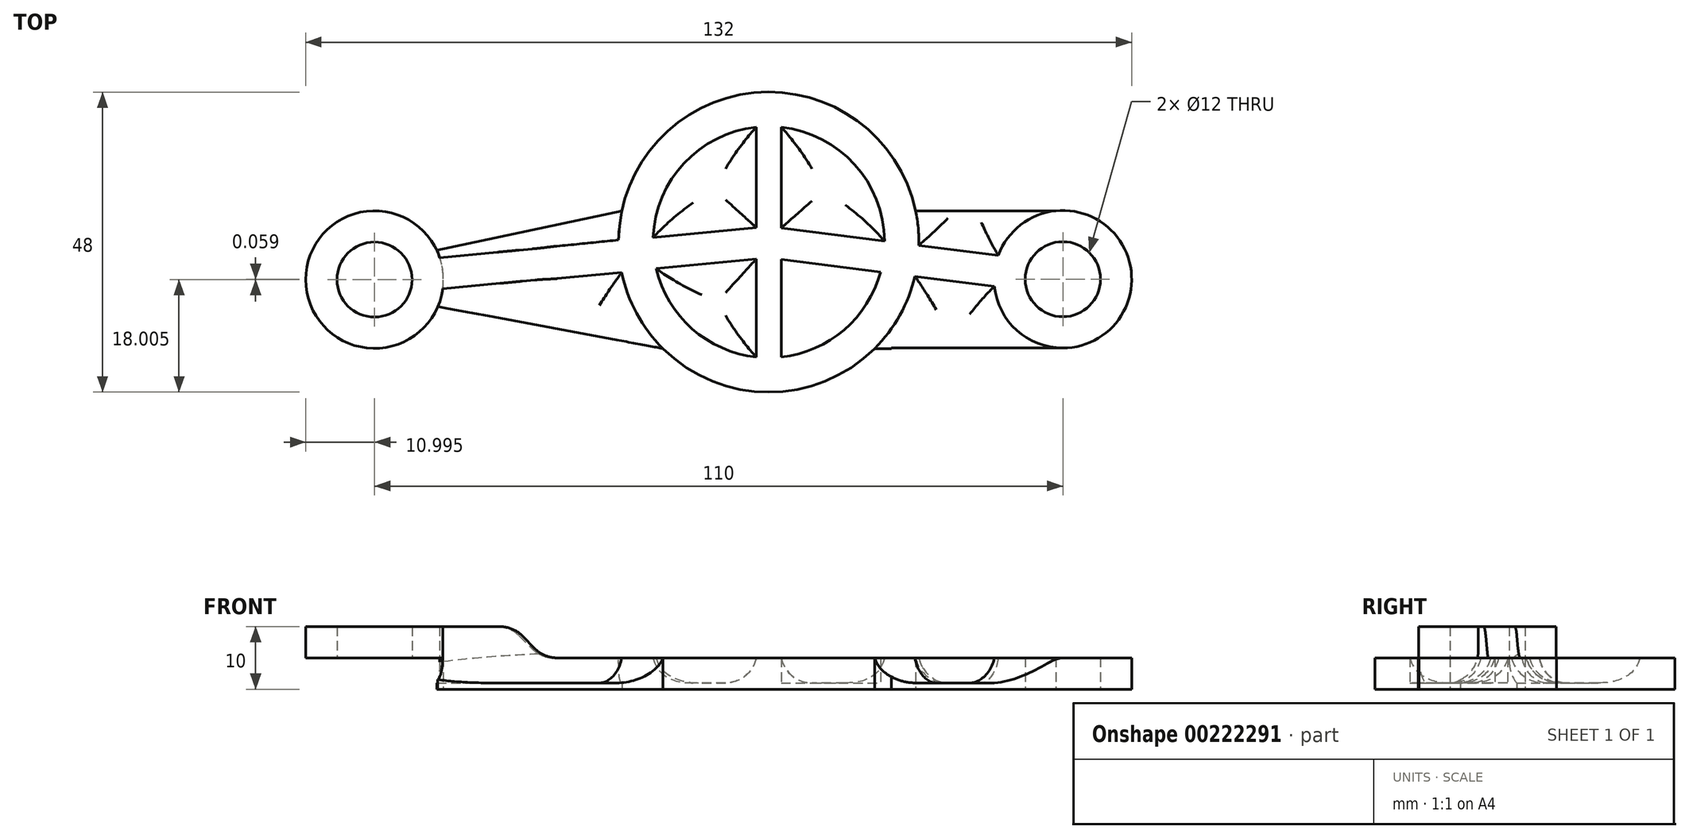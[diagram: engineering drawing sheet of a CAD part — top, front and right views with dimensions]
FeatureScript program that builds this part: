
annotation { "Feature Type Name" : "Feature", "Feature Type Description" : "" }
export const myFeature = defineFeature(function(context is Context, id is Id, definition is map)
    precondition{}
    {
        {
            var Q0;
            Q0=qCreatedBy(makeId("Top.planeOp"),FACE);
            var sketch = newSketch(context, id + "F0", { "sketchPlane" : qUnion([Q0])});
            skCircle(sketch, "E0", {"center": v(60.37, 19.35) * mm, "radius": 6 * mm});
            skLineSegment(sketch, "E1", {"start": v(-49.54, 25.3) * mm, "end": v(61.21, 25.3) * mm, "construction": true});
            skArc(sketch, "E2", {"start": v(60.37, 8.35) * mm, "mid": v(71.35, 19.93) * mm, "end": v(59.22, 30.3) * mm});
            skLineSegment(sketch, "E3.bottom", {"start": v(-10.1, 30.3) * mm, "end": v(32.97, 30.3) * mm});
            skLineSegment(sketch, "E3.top", {"start": v(-3.55, 8.27) * mm, "end": v(32.97, 8.27) * mm});
            skLineSegment(sketch, "E4.bottom", {"start": v(60.37, 8.35) * mm, "end": v(32.97, 8.35) * mm});
            skLineSegment(sketch, "E4.top", {"start": v(60.37, 30.3) * mm, "end": v(32.97, 30.3) * mm});
            skLineSegment(sketch, "E4.left", {"start": v(60.37, 25.3) * mm, "end": v(60.37, 25.35) * mm});
            skLineSegment(sketch, "E5.trimOffspring", {"start": v(32.97, 8.35) * mm, "end": v(32.97, 8.27) * mm});
            skLineSegment(sketch, "E6.trimOffspring", {"start": v(-49.63, 8.3) * mm, "end": v(-49.63, 8.27) * mm});
            skCircle(sketch, "E7", {"center": v(13.37, 25.3) * mm, "radius": 19 * mm, "construction": true});
            skArc(sketch, "E8", {"start": v(-3.55, 8.27) * mm, "mid": v(13.37, 1.3) * mm, "end": v(30.28, 8.27) * mm});
            skArc(sketch, "E9.trimOffspring", {"start": v(36.84, 30.3) * mm, "mid": v(13.37, 49.3) * mm, "end": v(-10.1, 30.3) * mm});
            skLineSegment(sketch, "E10", {"start": v(13.37, 25.3) * mm, "end": v(-49.63, 19.3) * mm, "construction": true});
            skLineSegment(sketch, "E11", {"start": v(-49.63, 19.3) * mm, "end": v(-49.4, 16.8) * mm});
            skLineSegment(sketch, "E12", {"start": v(-39.68, 23.97) * mm, "end": v(-10.1, 30.3) * mm});
            skLineSegment(sketch, "E13", {"start": v(-39.52, 14.97) * mm, "end": v(-3.55, 8.27) * mm});
            skArc(sketch, "E14", {"start": v(-39.52, 14.97) * mm, "mid": v(-38.64, 19.48) * mm, "end": v(-39.68, 23.97) * mm});
            skSolve(sketch);
        }
        {
            var Q0;
            Q0 = qSketchRegion(id + "F0", true);
            extrude(context, id + "F1", {"entities" : qUnion([Q0]), "depth" : 1 * mm});
        }
        {
            var Q0;
            Q0=makeQuery(id+"F1.opExtrude","CAP_FACE",FACE,{"disambiguationData":[OSD([sQuery(id+"F0.wireOp",EDGE,"2d779d73-95e5-4ba3-8006-2094022f3e68"),sQuery(id+"F0.wireOp",EDGE,"E0"),sQuery(id+"F0.wireOp",EDGE,"E2"),sQuery(id+"F0.wireOp",EDGE,"44cde904-ac06-42cb-a7ef-0284b28cecda"),sQuery(id+"F0.wireOp",EDGE,"E3.bottom"),sQuery(id+"F0.wireOp",EDGE,"E3.top"),sQuery(id+"F0.wireOp",EDGE,"E4.bottom"),sQuery(id+"F0.wireOp",EDGE,"E4.top"),sQuery(id+"F0.wireOp",EDGE,"E5.trimOffspring"),sQuery(id+"F0.wireOp",EDGE,"E6.trimOffspring"),sQuery(id+"F0.wireOp",EDGE,"E8"),sQuery(id+"F0.wireOp",EDGE,"E9.trimOffspring")])],"isStart":false});
            var sketch = newSketch(context, id + "F2", { "sketchPlane" : qUnion([Q0])});
            skLineSegment(sketch, "E15", {"start": v(-49.63, 19.3) * mm, "end": v(60.37, 19.35) * mm, "construction": true});
            skLineSegment(sketch, "E16", {"start": v(13.37, 1.3) * mm, "end": v(13.37, 49.3) * mm, "construction": true});
            skLineSegment(sketch, "E17", {"start": v(15.37, 43.69) * mm, "end": v(15.37, 27.56) * mm});
            skLineSegment(sketch, "E18", {"start": v(11.37, 6.9) * mm, "end": v(11.37, 22.6) * mm});
            skArc(sketch, "E19", {"start": v(-10.16, 20.54) * mm, "mid": v(13, 1.3) * mm, "end": v(36.73, 19.82) * mm});
            skArc(sketch, "E20", {"start": v(11.37, 43.69) * mm, "mid": v(-0.15, 37.93) * mm, "end": v(-5.12, 26.05) * mm});
            skLineSegment(sketch, "E21", {"start": v(13.37, 25.3) * mm, "end": v(60.37, 19.35) * mm, "construction": true});
            skLineSegment(sketch, "E22", {"start": v(13.37, 25.3) * mm, "end": v(-49.63, 19.3) * mm, "construction": true});
            skLineSegment(sketch, "E23.trimOffspring", {"start": v(11.37, 49.21) * mm, "end": v(11.37, 49.3) * mm});
            skArc(sketch, "E24.trimOffspring", {"start": v(15.37, 6.9) * mm, "mid": v(25.4, 11.25) * mm, "end": v(31.24, 20.52) * mm});
            skLineSegment(sketch, "E25", {"start": v(-39.2, 22.8) * mm, "end": v(-10.63, 25.52) * mm});
            skLineSegment(sketch, "E26", {"start": v(11.37, 22.6) * mm, "end": v(-4.65, 21.07) * mm});
            skCircle(sketch, "E27", {"center": v(-49.63, 19.3) * mm, "radius": 6 * mm});
            skArc(sketch, "E28", {"start": v(-39.2, 22.8) * mm, "mid": v(-60.59, 18.25) * mm, "end": v(-38.73, 17.82) * mm});
            skArc(sketch, "E29.trimOffspring", {"start": v(-4.65, 21.07) * mm, "mid": v(1.1, 11.44) * mm, "end": v(11.37, 6.9) * mm});
            skLineSegment(sketch, "E30.trimOffspring", {"start": v(-5.12, 26.05) * mm, "end": v(11.37, 27.62) * mm});
            skLineSegment(sketch, "E31.trimOffspring", {"start": v(-10.16, 20.54) * mm, "end": v(-38.73, 17.82) * mm});
            skLineSegment(sketch, "E32.trimOffspring", {"start": v(11.37, 27.62) * mm, "end": v(11.37, 43.69) * mm});
            skLineSegment(sketch, "E33", {"start": v(15.37, 22.52) * mm, "end": v(49.42, 18.22) * mm});
            skLineSegment(sketch, "E34.trimOffspring", {"start": v(15.37, 22.52) * mm, "end": v(15.37, 6.9) * mm});
            skArc(sketch, "E35.trimOffspring", {"start": v(31.86, 25.48) * mm, "mid": v(27.07, 37.72) * mm, "end": v(15.37, 43.69) * mm});
            skArc(sketch, "E36.trimOffspring", {"start": v(37.36, 24.78) * mm, "mid": v(13.73, 49.3) * mm, "end": v(-10.63, 25.52) * mm});
            skCircle(sketch, "E37", {"center": v(60.37, 19.35) * mm, "radius": 6 * mm});
            skArc(sketch, "E38.trimOffspring", {"start": v(49.42, 18.22) * mm, "mid": v(71.28, 17.98) * mm, "end": v(50.05, 23.18) * mm});
            skLineSegment(sketch, "E39.trimOffspring", {"start": v(50.05, 23.18) * mm, "end": v(15.37, 27.56) * mm});
            skSolve(sketch);
        }
        {
            var Q0;
            Q0=makeQuery(id+"F2.imprint","IMPRINT",FACE,{"disambiguationData":[TD([[makeQuery(id+"F2.imprint","IMPRINT",EDGE,{"derivedFrom":sQuery(id+"F2.wireOp",EDGE,"E17")}),-1.0]])]});
            extrude(context, id + "F3", {"entities" : qUnion([Q0]), "operationType" : NewBodyOperationType.ADD, "depth" : 4 * mm});
        }
        {
            var Q0;
            Q0=makeQuery(id+"F3.opExtrude","CAP_FACE",FACE,{"disambiguationData":[OSD([sQuery(id+"F2.wireOp",EDGE,"E17"),sQuery(id+"F2.wireOp",EDGE,"E18"),sQuery(id+"F2.wireOp",EDGE,"E19"),sQuery(id+"F2.wireOp",EDGE,"E20"),sQuery(id+"F2.wireOp",EDGE,"E24.trimOffspring"),sQuery(id+"F2.wireOp",EDGE,"E25"),sQuery(id+"F2.wireOp",EDGE,"E26"),sQuery(id+"F2.wireOp",EDGE,"E27"),sQuery(id+"F2.wireOp",EDGE,"E28"),sQuery(id+"F2.wireOp",EDGE,"E29.trimOffspring"),sQuery(id+"F2.wireOp",EDGE,"E30.trimOffspring"),sQuery(id+"F2.wireOp",EDGE,"E31.trimOffspring"),sQuery(id+"F2.wireOp",EDGE,"E32.trimOffspring"),sQuery(id+"F2.wireOp",EDGE,"E33"),sQuery(id+"F2.wireOp",EDGE,"E34.trimOffspring"),sQuery(id+"F2.wireOp",EDGE,"E35.trimOffspring"),sQuery(id+"F2.wireOp",EDGE,"E36.trimOffspring"),sQuery(id+"F2.wireOp",EDGE,"E37"),sQuery(id+"F2.wireOp",EDGE,"E38.trimOffspring"),sQuery(id+"F2.wireOp",EDGE,"E39.trimOffspring")])],"isStart":false});
            var sketch = newSketch(context, id + "F4", { "sketchPlane" : qUnion([Q0])});
            skCircle(sketch, "E40", {"center": v(-49.63, 19.3) * mm, "radius": 6 * mm});
            skArc(sketch, "E41", {"start": v(-39.2, 22.8) * mm, "mid": v(-60.59, 18.25) * mm, "end": v(-38.73, 17.82) * mm});
            skLineSegment(sketch, "E42", {"start": v(-38.73, 17.82) * mm, "end": v(-22.52, 19.37) * mm});
            skLineSegment(sketch, "E43", {"start": v(-22.52, 19.37) * mm, "end": v(-23, 24.34) * mm});
            skLineSegment(sketch, "E44", {"start": v(-23, 24.34) * mm, "end": v(-39.2, 22.8) * mm});
            skSolve(sketch);
        }
        {
            var Q0;
            Q0 = qSketchRegion(id + "F4", true);
            extrude(context, id + "F5", {"entities" : qUnion([Q0]), "operationType" : NewBodyOperationType.ADD, "depth" : 5 * mm});
        }
        {
            var Q0;
            Q0=makeQuery(id+"F5.opExtrude","CAP_EDGE",EDGE,{"disambiguationData":[OSD([sQuery(id+"F4.wireOp",EDGE,"E43")])],"isStart":false});
            chamfer(context, id + "F6", {"entities" : qUnion([Q0]), "width" : 5 * mm, "tangentPropagation" : true});
        }
        {
            var Q0;
            Q0=makeQuery(id+"F1.opExtrude","CAP_FACE",FACE,{"disambiguationData":[OSD([sQuery(id+"F0.wireOp",EDGE,"2d779d73-95e5-4ba3-8006-2094022f3e68"),sQuery(id+"F0.wireOp",EDGE,"E0"),sQuery(id+"F0.wireOp",EDGE,"E2"),sQuery(id+"F0.wireOp",EDGE,"44cde904-ac06-42cb-a7ef-0284b28cecda"),sQuery(id+"F0.wireOp",EDGE,"E3.bottom"),sQuery(id+"F0.wireOp",EDGE,"E3.top"),sQuery(id+"F0.wireOp",EDGE,"E4.bottom"),sQuery(id+"F0.wireOp",EDGE,"E4.top"),sQuery(id+"F0.wireOp",EDGE,"E5.trimOffspring"),sQuery(id+"F0.wireOp",EDGE,"E6.trimOffspring"),sQuery(id+"F0.wireOp",EDGE,"E8"),sQuery(id+"F0.wireOp",EDGE,"E9.trimOffspring")])],"isStart":true});
            var sketch = newSketch(context, id + "F7", { "sketchPlane" : qUnion([Q0])});
            skCircle(sketch, "E45", {"center": v(-49.63, -19.3) * mm, "radius": 6 * mm});
            skCircle(sketch, "E46", {"center": v(-49.63, -19.3) * mm, "radius": 11 * mm});
            skSolve(sketch);
        }
        {
            var Q0;
            Q0=makeQuery(id+"F7.imprint","IMPRINT",FACE,{"disambiguationData":[TD([[makeQuery(id+"F7.imprint","IMPRINT",EDGE,{"derivedFrom":sQuery(id+"F7.wireOp",EDGE,"E45")}),1.0]])]});
            extrude(context, id + "F8", {"entities" : qUnion([Q0]), "operationType" : NewBodyOperationType.REMOVE, "oppositeDirection" : true, "depth" : 5 * mm});
        }
        {
            var Q0;
            Q0=makeQuery(id+"F3.opExtrude","CAP_EDGE",EDGE,{"disambiguationData":[OSD([sQuery(id+"F2.wireOp",EDGE,"E20")])],"isStart":true});
            var Q1;
            Q1=makeQuery(id+"F3.opExtrude","CAP_EDGE",EDGE,{"disambiguationData":[OSD([sQuery(id+"F2.wireOp",EDGE,"E35.trimOffspring")])],"isStart":true});
            var Q2;
            Q2=makeQuery(id+"F3.opExtrude","CAP_EDGE",EDGE,{"disambiguationData":[OSD([sQuery(id+"F2.wireOp",EDGE,"E29.trimOffspring")])],"isStart":true});
            var Q3;
            Q3=makeQuery(id+"F3.opExtrude","CAP_EDGE",EDGE,{"disambiguationData":[OSD([sQuery(id+"F2.wireOp",EDGE,"E24.trimOffspring")])],"isStart":true});
            var Q4;
            Q4=makeQuery(id+"F3.opExtrude","CAP_EDGE",EDGE,{"disambiguationData":[OSD([sQuery(id+"F2.wireOp",EDGE,"E30.trimOffspring")])],"isStart":true});
            var Q5;
            {var subQ0=sQuery(id+"F2.wireOp",EDGE,"E39.trimOffspring");Q5=makeQuery(id+"F3.opExtrude","CAP_EDGE",EDGE,{"disambiguationData":[OSD([subQ0]),TDD([makeQuery(id+"F2.imprint","IMPRINT",EDGE,{"disambiguationData":[TD([[makeQuery(id+"F2.imprint","INTERSECT",VERTEX,{"derivedFrom":[sQuery(id+"F2.wireOp",EDGE,"E17"),subQ0]}),1.0]])],"derivedFrom":subQ0})])],"isStart":true});}
            var Q6;
            Q6=makeQuery(id+"F3.opExtrude","CAP_EDGE",EDGE,{"disambiguationData":[OSD([sQuery(id+"F2.wireOp",EDGE,"E18")])],"isStart":true});
            var Q7;
            Q7=makeQuery(id+"F3.opExtrude","CAP_EDGE",EDGE,{"disambiguationData":[OSD([sQuery(id+"F2.wireOp",EDGE,"E32.trimOffspring")])],"isStart":true});
            var Q8;
            Q8=makeQuery(id+"F3.opExtrude","CAP_EDGE",EDGE,{"disambiguationData":[OSD([sQuery(id+"F2.wireOp",EDGE,"E17")])],"isStart":true});
            var Q9;
            Q9=makeQuery(id+"F3.opExtrude","CAP_EDGE",EDGE,{"disambiguationData":[OSD([sQuery(id+"F2.wireOp",EDGE,"E34.trimOffspring")])],"isStart":true});
            var Q10;
            Q10=makeQuery(id+"F3.opExtrude","CAP_EDGE",EDGE,{"disambiguationData":[OSD([sQuery(id+"F2.wireOp",EDGE,"E26")])],"isStart":true});
            var Q11;
            {var subQ0=sQuery(id+"F2.wireOp",EDGE,"E33");Q11=makeQuery(id+"F3.opExtrude","CAP_EDGE",EDGE,{"disambiguationData":[OSD([subQ0]),TDD([makeQuery(id+"F2.imprint","IMPRINT",EDGE,{"disambiguationData":[TD([[makeQuery(id+"F2.imprint","INTERSECT",VERTEX,{"derivedFrom":[sQuery(id+"F2.wireOp",EDGE,"E24.trimOffspring"),subQ0]}),1.0]])],"derivedFrom":subQ0})])],"isStart":true});}
            var Q12;
            Q12=makeQuery(id+"F3.opExtrude","CAP_EDGE",EDGE,{"disambiguationData":[OSD([sQuery(id+"F2.wireOp",EDGE,"E31.trimOffspring")])],"isStart":true});
            var Q13;
            {var subQ0=sQuery(id+"F2.wireOp",EDGE,"E19");Q13=makeQuery(id+"F3.boolean.opBoolean","SPLIT",EDGE,{"disambiguationData":[TD([makeQuery(id+"F3.opExtrude","SWEPT_FACE",FACE,{"disambiguationData":[OSD([sQuery(id+"F2.wireOp",EDGE,"E31.trimOffspring")])]})])],"derivedFrom":makeQuery(id+"F3.opExtrude","CAP_EDGE",EDGE,{"disambiguationData":[OSD([subQ0])],"isStart":true})});}
            var Q14;
            {var subQ0=sQuery(id+"F2.wireOp",EDGE,"E19");var subQ2=sQuery(id+"F0.wireOp",EDGE,"E5.trimOffspring");var subQ3=sQuery(id+"F0.wireOp",EDGE,"E3.top");Q14=makeQuery(id+"F3.boolean.opBoolean","SPLIT",EDGE,{"disambiguationData":[TD([makeQuery(id+"F1.opExtrude","SWEPT_FACE",FACE,{"disambiguationData":[OSD([subQ3]),TDD([makeQuery(id+"F0.imprint","IMPRINT",EDGE,{"disambiguationData":[TD([[makeQuery(id+"F0.imprint","INTERSECT",VERTEX,{"derivedFrom":[subQ3,subQ2]}),1.0]])],"derivedFrom":subQ3})])]})])],"derivedFrom":makeQuery(id+"F3.opExtrude","CAP_EDGE",EDGE,{"disambiguationData":[OSD([subQ0])],"isStart":true})});}
            var Q15;
            {var subQ0=sQuery(id+"F2.wireOp",EDGE,"E33");Q15=makeQuery(id+"F3.opExtrude","CAP_EDGE",EDGE,{"disambiguationData":[OSD([subQ0]),TDD([makeQuery(id+"F2.imprint","IMPRINT",EDGE,{"disambiguationData":[TD([[makeQuery(id+"F2.imprint","INTERSECT",VERTEX,{"derivedFrom":[sQuery(id+"F2.wireOp",EDGE,"E19"),subQ0]}),-1.0]])],"derivedFrom":subQ0})])],"isStart":true});}
            var Q16;
            {var subQ1=sQuery(id+"F2.wireOp",EDGE,"E38.trimOffspring");var subQ3=sQuery(id+"F0.wireOp",EDGE,"E4.bottom");Q16=makeQuery(id+"F3.boolean.opBoolean","SPLIT",EDGE,{"disambiguationData":[TD([makeQuery(id+"F1.opExtrude","SWEPT_FACE",FACE,{"disambiguationData":[OSD([subQ3])]})])],"derivedFrom":makeQuery(id+"F3.opExtrude","CAP_EDGE",EDGE,{"disambiguationData":[OSD([subQ1])],"isStart":true})});}
            var Q17;
            Q17=makeQuery(id+"F3.opExtrude","CAP_EDGE",EDGE,{"disambiguationData":[OSD([sQuery(id+"F2.wireOp",EDGE,"E25")])],"isStart":true});
            var Q18;
            {var subQ1=sQuery(id+"F0.wireOp",EDGE,"E3.bottom");var subQ2=sQuery(id+"F2.wireOp",EDGE,"E36.trimOffspring");Q18=makeQuery(id+"F3.boolean.opBoolean","SPLIT",EDGE,{"disambiguationData":[TD([makeQuery(id+"F1.opExtrude","SWEPT_FACE",FACE,{"disambiguationData":[OSD([subQ1])]})])],"derivedFrom":makeQuery(id+"F3.opExtrude","CAP_EDGE",EDGE,{"disambiguationData":[OSD([subQ2])],"isStart":true})});}
            var Q19;
            {var subQ0=sQuery(id+"F0.wireOp",EDGE,"E4.top");var subQ1=sQuery(id+"F2.wireOp",EDGE,"E38.trimOffspring");Q19=makeQuery(id+"F3.boolean.opBoolean","SPLIT",EDGE,{"disambiguationData":[TD([makeQuery(id+"F1.opExtrude","SWEPT_FACE",FACE,{"disambiguationData":[OSD([subQ0])]})])],"derivedFrom":makeQuery(id+"F3.opExtrude","CAP_EDGE",EDGE,{"disambiguationData":[OSD([subQ1])],"isStart":true})});}
            var Q20;
            {var subQ0=sQuery(id+"F2.wireOp",EDGE,"E39.trimOffspring");Q20=makeQuery(id+"F3.opExtrude","CAP_EDGE",EDGE,{"disambiguationData":[OSD([subQ0]),TDD([makeQuery(id+"F2.imprint","IMPRINT",EDGE,{"disambiguationData":[TD([[makeQuery(id+"F2.imprint","INTERSECT",VERTEX,{"derivedFrom":[sQuery(id+"F2.wireOp",EDGE,"E38.trimOffspring"),subQ0]}),-1.0]])],"derivedFrom":subQ0})])],"isStart":true});}
            var Q21;
            {var subQ0=sQuery(id+"F2.wireOp",EDGE,"E36.trimOffspring");var subQ2=sQuery(id+"F0.wireOp",EDGE,"E4.top");Q21=makeQuery(id+"F3.boolean.opBoolean","SPLIT",EDGE,{"disambiguationData":[TD([makeQuery(id+"F1.opExtrude","SWEPT_FACE",FACE,{"disambiguationData":[OSD([subQ2])]})])],"derivedFrom":makeQuery(id+"F3.opExtrude","CAP_EDGE",EDGE,{"disambiguationData":[OSD([subQ0])],"isStart":true})});}
            var Q22;
            {var subQ0=sQuery(id+"F4.wireOp",EDGE,"E43");Q22=makeQuery(id+"F6.opChamfer","BLEND_EDGE",EDGE,{"blendedFrom":[makeQuery(id+"F5.opExtrude","CAP_EDGE",EDGE,{"disambiguationData":[OSD([subQ0])],"isStart":false}),makeQuery(id+"F5.opExtrude","CAP_FACE",FACE,{"disambiguationData":[OSD([sQuery(id+"F4.wireOp",EDGE,"E40"),sQuery(id+"F4.wireOp",EDGE,"E41"),sQuery(id+"F4.wireOp",EDGE,"E42"),subQ0,sQuery(id+"F4.wireOp",EDGE,"E44")])],"isStart":false})],"blendedInto":[makeQuery(id+"F5.opExtrude","CAP_FACE",FACE,{"disambiguationData":[OSD([sQuery(id+"F4.wireOp",EDGE,"E40"),sQuery(id+"F4.wireOp",EDGE,"E41"),sQuery(id+"F4.wireOp",EDGE,"E42"),subQ0,sQuery(id+"F4.wireOp",EDGE,"E44")])],"isStart":false})]});}
            fillet(context, id + "F9", {"entities" : qUnion([Q0, Q1, Q2, Q3, Q4, Q5, Q6, Q7, Q8, Q9, Q10, Q11, Q12, Q13, Q14, Q15, Q16, Q17, Q18, Q19, Q20, Q21, Q22]), "radius" : 5 * mm, "tangentPropagation" : true, "allowEdgeOverflow" : false});
        }
        {
            var Q0;
            Q0=makeQuery(id+"F6.opChamfer","BLEND_EDGE",EDGE,{"blendedFrom":[makeQuery(id+"F5.opExtrude","CAP_EDGE",EDGE,{"disambiguationData":[OSD([sQuery(id+"F4.wireOp",EDGE,"E43")])],"isStart":false}),makeQuery(id+"F3.opExtrude","CAP_FACE",FACE,{"disambiguationData":[OSD([sQuery(id+"F2.wireOp",EDGE,"E17"),sQuery(id+"F2.wireOp",EDGE,"E18"),sQuery(id+"F2.wireOp",EDGE,"E19"),sQuery(id+"F2.wireOp",EDGE,"E20"),sQuery(id+"F2.wireOp",EDGE,"E24.trimOffspring"),sQuery(id+"F2.wireOp",EDGE,"E25"),sQuery(id+"F2.wireOp",EDGE,"E26"),sQuery(id+"F2.wireOp",EDGE,"E27"),sQuery(id+"F2.wireOp",EDGE,"E28"),sQuery(id+"F2.wireOp",EDGE,"E29.trimOffspring"),sQuery(id+"F2.wireOp",EDGE,"E30.trimOffspring"),sQuery(id+"F2.wireOp",EDGE,"E31.trimOffspring"),sQuery(id+"F2.wireOp",EDGE,"E32.trimOffspring"),sQuery(id+"F2.wireOp",EDGE,"E33"),sQuery(id+"F2.wireOp",EDGE,"E34.trimOffspring"),sQuery(id+"F2.wireOp",EDGE,"E35.trimOffspring"),sQuery(id+"F2.wireOp",EDGE,"E36.trimOffspring"),sQuery(id+"F2.wireOp",EDGE,"E37"),sQuery(id+"F2.wireOp",EDGE,"E38.trimOffspring"),sQuery(id+"F2.wireOp",EDGE,"E39.trimOffspring")])],"isStart":false})],"blendedInto":[makeQuery(id+"F3.opExtrude","CAP_FACE",FACE,{"disambiguationData":[OSD([sQuery(id+"F2.wireOp",EDGE,"E17"),sQuery(id+"F2.wireOp",EDGE,"E18"),sQuery(id+"F2.wireOp",EDGE,"E19"),sQuery(id+"F2.wireOp",EDGE,"E20"),sQuery(id+"F2.wireOp",EDGE,"E24.trimOffspring"),sQuery(id+"F2.wireOp",EDGE,"E25"),sQuery(id+"F2.wireOp",EDGE,"E26"),sQuery(id+"F2.wireOp",EDGE,"E27"),sQuery(id+"F2.wireOp",EDGE,"E28"),sQuery(id+"F2.wireOp",EDGE,"E29.trimOffspring"),sQuery(id+"F2.wireOp",EDGE,"E30.trimOffspring"),sQuery(id+"F2.wireOp",EDGE,"E31.trimOffspring"),sQuery(id+"F2.wireOp",EDGE,"E32.trimOffspring"),sQuery(id+"F2.wireOp",EDGE,"E33"),sQuery(id+"F2.wireOp",EDGE,"E34.trimOffspring"),sQuery(id+"F2.wireOp",EDGE,"E35.trimOffspring"),sQuery(id+"F2.wireOp",EDGE,"E36.trimOffspring"),sQuery(id+"F2.wireOp",EDGE,"E37"),sQuery(id+"F2.wireOp",EDGE,"E38.trimOffspring"),sQuery(id+"F2.wireOp",EDGE,"E39.trimOffspring")])],"isStart":false})]});
            fillet(context, id + "F10", {"entities" : qUnion([Q0]), "radius" : 5 * mm, "tangentPropagation" : true, "allowEdgeOverflow" : false});
        }
    });
